# Revit family: 02411-G01 (Rev A), Assembly, Takeoff, Flat Duct, Twist-Fit, 2in
name_source: partatom
category: Duct Accessories
units: mm (PartAtom-declared; Revit-internal decimal feet)

## family parameters
Always vertical = No
Cut with Voids When Loaded = No
OmniClass Number = 23.75.70.00
OmniClass Title = HVAC Distribution Devices
Part Type = Attaches To
Round Connector Dimension = Use Diameter
Shared = No
Work Plane-Based = Yes

## types (1)
- UPC-28TF-1
    Assembly Code = D3040100
    Default Elevation = 48"
    Description = 1 TAKE-OFF, 2 DIA X FLAT METAL DUCT, TFS
    Diameter = 5"
    Finish = Paint - Unico - White
    Keynote = 23 30 00
    Manufacturer = Unico, Inc.
    Manufacturer Fax Number = 314-457-9000
    Model = UPC-28TF-1
    Performance URL = https://www.unicosystem.com
    Product Page URL = https://shop.unicosystem.com
    URL = https://www.unicosystem.com
    Version = 2020 - v1.0a
    Video Link = https://www.youtube.com
    Warranty URL = https://www.unicosystem.com

## geometry (parser evidence)
native form markers: Sweep x4
no freeform markers — native parametric forms only
